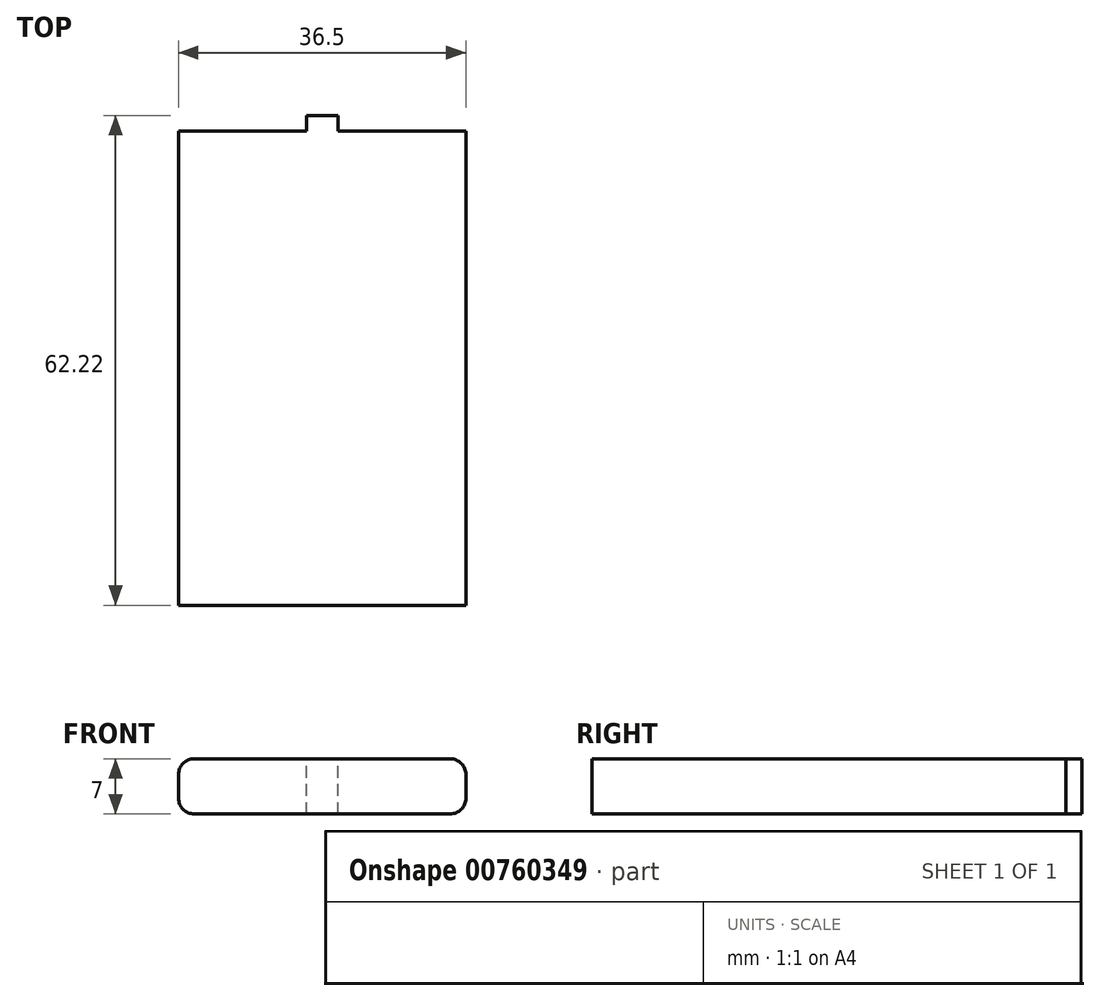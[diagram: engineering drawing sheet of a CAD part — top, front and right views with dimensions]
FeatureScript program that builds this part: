
annotation { "Feature Type Name" : "Feature", "Feature Type Description" : "" }
export const myFeature = defineFeature(function(context is Context, id is Id, definition is map)
    precondition{}
    {
        {
            var Q0;
            Q0=qCreatedBy(makeId("Top.planeOp"),FACE);
            var sketch = newSketch(context, id + "F0", { "sketchPlane" : qUnion([Q0])});
            skLineSegment(sketch, "E0.bottom", {"start": v(18.25, 30.11) * mm, "end": v(-18.25, 30.11) * mm});
            skLineSegment(sketch, "E0.top", {"start": v(18.25, -30.11) * mm, "end": v(-18.25, -30.11) * mm});
            skLineSegment(sketch, "E0.left", {"start": v(18.25, 30.11) * mm, "end": v(18.25, -30.11) * mm});
            skLineSegment(sketch, "E0.right", {"start": v(-18.25, 30.11) * mm, "end": v(-18.25, -30.11) * mm});
            skPoint(sketch, "E0.middle", {"position": v(0, 0) * mm});
            skSolve(sketch);
        }
        {
            var Q0;
            Q0=makeQuery(id+"F0.imprint","IMPRINT",FACE,{"disambiguationData":[TD([[makeQuery(id+"F0.imprint","IMPRINT",EDGE,{"derivedFrom":sQuery(id+"F0.wireOp",EDGE,"E0.bottom")}),1.0]])]});
            extrude(context, id + "F1", {"entities" : qUnion([Q0]), "depth" : 7 * mm, "offsetDistance" : 25 * mm});
        }
        {
            var Q0;
            Q0=makeQuery(id+"F1.opExtrude","SWEPT_FACE",FACE,{"disambiguationData":[OSD([sQuery(id+"F0.wireOp",EDGE,"E0.bottom")])]});
            var sketch = newSketch(context, id + "F2", { "sketchPlane" : qUnion([Q0])});
            skLineSegment(sketch, "E1.bottom", {"start": v(2, 0) * mm, "end": v(-2, 0) * mm});
            skLineSegment(sketch, "E1.top", {"start": v(2, 7) * mm, "end": v(-2, 7) * mm});
            skLineSegment(sketch, "E1.left", {"start": v(2, 0) * mm, "end": v(2, 7) * mm});
            skLineSegment(sketch, "E1.right", {"start": v(-2, 0) * mm, "end": v(-2, 7) * mm});
            skLineSegment(sketch, "E2", {"start": v(0, 0) * mm, "end": v(0, 7) * mm, "construction": true});
            skSolve(sketch);
        }
        {
            var Q0;
            Q0 = qSketchRegion(id + "F2", true);
            extrude(context, id + "F3", {"entities" : qUnion([Q0]), "operationType" : NewBodyOperationType.ADD, "depth" : 2 * mm, "offsetDistance" : 25 * mm});
        }
        {
            var Q0;
            Q0=makeQuery(id+"F1.opExtrude","CAP_EDGE",EDGE,{"disambiguationData":[OSD([sQuery(id+"F0.wireOp",EDGE,"E0.left")])],"isStart":false});
            var Q1;
            Q1=makeQuery(id+"F1.opExtrude","CAP_EDGE",EDGE,{"disambiguationData":[OSD([sQuery(id+"F0.wireOp",EDGE,"E0.left")])],"isStart":true});
            var Q2;
            Q2=makeQuery(id+"F1.opExtrude","CAP_EDGE",EDGE,{"disambiguationData":[OSD([sQuery(id+"F0.wireOp",EDGE,"E0.right")])],"isStart":false});
            var Q3;
            Q3=makeQuery(id+"F1.opExtrude","CAP_EDGE",EDGE,{"disambiguationData":[OSD([sQuery(id+"F0.wireOp",EDGE,"E0.right")])],"isStart":true});
            fillet(context, id + "F4", {"entities" : qUnion([Q0, Q1, Q2, Q3]), "radius" : 2 * mm, "tangentPropagation" : true, "allowEdgeOverflow" : false});
        }
    });
